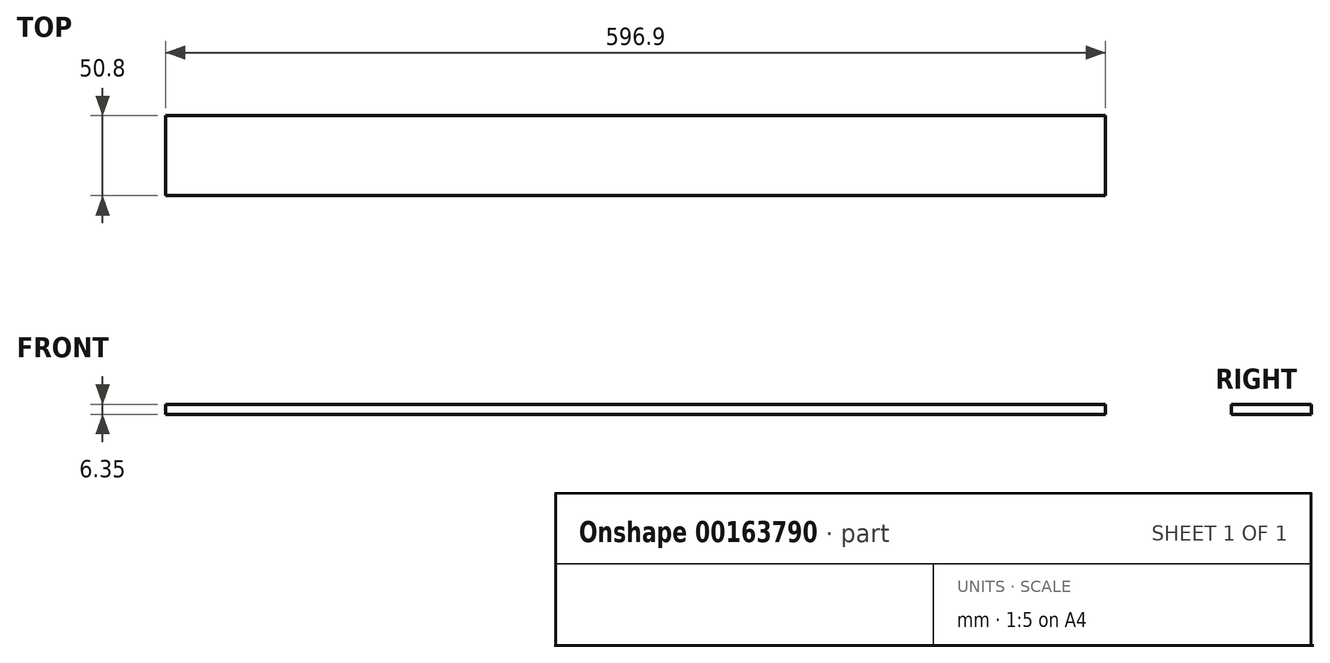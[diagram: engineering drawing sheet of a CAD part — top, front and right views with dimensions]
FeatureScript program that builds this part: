
annotation { "Feature Type Name" : "Feature", "Feature Type Description" : "" }
export const myFeature = defineFeature(function(context is Context, id is Id, definition is map)
    precondition{}
    {
        {
            var Q0;
            Q0=qCreatedBy(makeId("Top.planeOp"),FACE);
            var sketch = newSketch(context, id + "F0", { "sketchPlane" : qUnion([Q0])});
            skLineSegment(sketch, "E0.bottom", {"start": v(298.45, -25.4) * mm, "end": v(-298.45, -25.4) * mm});
            skLineSegment(sketch, "E0.top", {"start": v(298.45, 25.4) * mm, "end": v(-298.45, 25.4) * mm});
            skLineSegment(sketch, "E0.left", {"start": v(298.45, -25.4) * mm, "end": v(298.45, 25.4) * mm});
            skLineSegment(sketch, "E0.right", {"start": v(-298.45, -25.4) * mm, "end": v(-298.45, 25.4) * mm});
            skPoint(sketch, "E0.middle", {"position": v(0, 0) * mm});
            skSolve(sketch);
        }
        {
            var Q0;
            Q0 = qSketchRegion(id + "F0", true);
            extrude(context, id + "F1", {"entities" : qUnion([Q0]), "depth" : 6.35 * mm});
        }
    });
